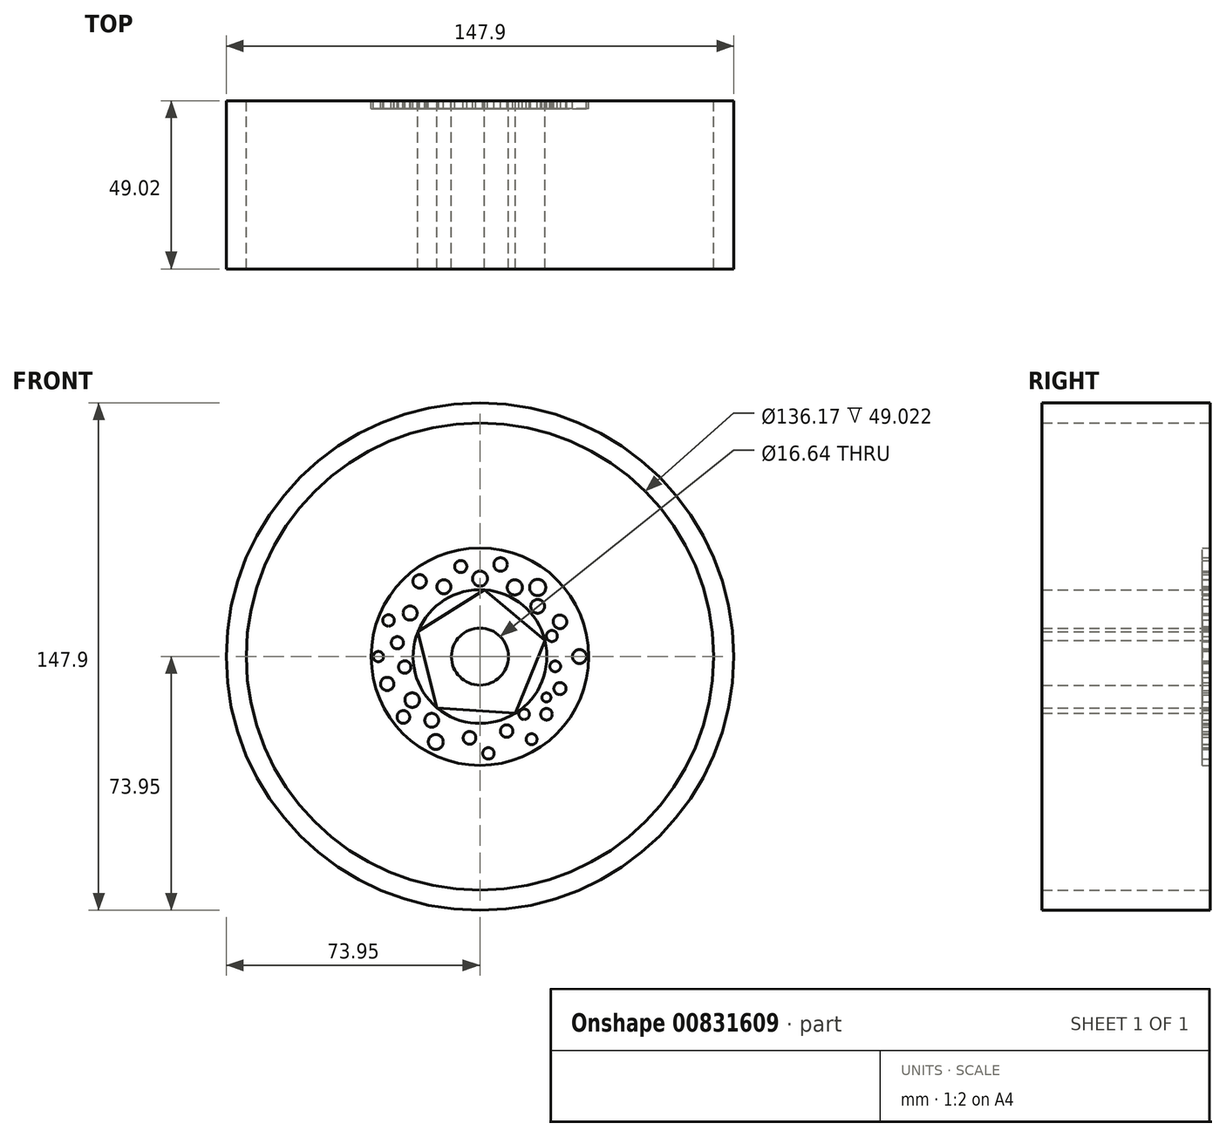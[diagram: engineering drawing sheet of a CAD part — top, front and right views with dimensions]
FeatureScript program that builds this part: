
annotation { "Feature Type Name" : "Feature", "Feature Type Description" : "" }
export const myFeature = defineFeature(function(context is Context, id is Id, definition is map)
    precondition{}
    {
        {
            var Q0;
            Q0=qCreatedBy(makeId("Front.planeOp"),FACE);
            var sketch = newSketch(context, id + "F0", { "sketchPlane" : qUnion([Q0])});
            skCircle(sketch, "E0", {"center": v(0, 0) * mm, "radius": 73.95 * mm});
            skCircle(sketch, "E1", {"center": v(0, 0) * mm, "radius": 68.08 * mm});
            skCircle(sketch, "E2.cCircle", {"center": v(0, 0) * mm, "radius": 15.77 * mm, "construction": true});
            skLineSegment(sketch, "E2.0", {"start": v(1.34, 19.45) * mm, "end": v(18.91, 4.73) * mm});
            skLineSegment(sketch, "E2.1", {"start": v(18.91, 4.73) * mm, "end": v(10.35, -16.52) * mm});
            skLineSegment(sketch, "E2.2", {"start": v(10.35, -16.52) * mm, "end": v(-12.52, -14.95) * mm});
            skLineSegment(sketch, "E2.3", {"start": v(-12.52, -14.95) * mm, "end": v(-18.08, 7.29) * mm});
            skLineSegment(sketch, "E2.4", {"start": v(-18.08, 7.29) * mm, "end": v(1.34, 19.45) * mm});
            skPoint(sketch, "E2.0.midPoint", {"position": v(10.13, 12.1) * mm});
            skPoint(sketch, "E3.orphan", {"position": v(68.08, 0) * mm});
            skPoint(sketch, "E4.end.orphan", {"position": v(0, 68.08) * mm});
            skCircle(sketch, "E5", {"center": v(0, 0) * mm, "radius": 8.32 * mm});
            skLineSegment(sketch, "E6", {"start": v(-2.6, 16.99) * mm, "end": v(12, 67.02) * mm});
            skLineSegment(sketch, "E7", {"start": v(6.2, 15.37) * mm, "end": v(14.3, 66.56) * mm});
            skLineSegment(sketch, "E8", {"start": v(14.3, 66.56) * mm, "end": v(12, 67.02) * mm});
            skLineSegment(sketch, "E9", {"start": v(-4.16, 16) * mm, "end": v(-31.83, 60.18) * mm});
            skLineSegment(sketch, "E10", {"start": v(-31.83, 60.18) * mm, "end": v(-34.5, 58.7) * mm});
            skLineSegment(sketch, "E11", {"start": v(-34.5, 58.7) * mm, "end": v(-12.64, 10.7) * mm});
            skLineSegment(sketch, "E12", {"start": v(-14.83, 9.32) * mm, "end": v(-62, 28.13) * mm});
            skLineSegment(sketch, "E13", {"start": v(-62, 28.13) * mm, "end": v(-64.05, 23.1) * mm});
            skLineSegment(sketch, "E14", {"start": v(-64.05, 23.1) * mm, "end": v(-16.26, 0) * mm});
            skLineSegment(sketch, "E15", {"start": v(-15.3, -3.83) * mm, "end": v(-60.76, -30.73) * mm});
            skLineSegment(sketch, "E16", {"start": v(-60.76, -30.73) * mm, "end": v(-58.22, -35.3) * mm});
            skLineSegment(sketch, "E17", {"start": v(-58.22, -35.3) * mm, "end": v(-12.52, -14.95) * mm});
            skLineSegment(sketch, "E18", {"start": v(-8.89, -15.2) * mm, "end": v(-20.94, -64.78) * mm});
            skPoint(sketch, "E19.end.orphan", {"position": v(-16.26, -67.05) * mm});
            skLineSegment(sketch, "E20", {"start": v(-16.26, -66.11) * mm, "end": v(2.9, -16) * mm});
            skLineSegment(sketch, "E21", {"start": v(23.8, -63.79) * mm, "end": v(27.6, -62.24) * mm});
            skLineSegment(sketch, "E22", {"start": v(49.88, -46.34) * mm, "end": v(53.15, -42.55) * mm});
            skLineSegment(sketch, "E23", {"start": v(67.23, -10.73) * mm, "end": v(67.82, -6.04) * mm});
            skLineSegment(sketch, "E24", {"start": v(59.94, 32.29) * mm, "end": v(56.36, 38.2) * mm});
            skLineSegment(sketch, "E25", {"start": v(8.55, -16.4) * mm, "end": v(33.9, -59.05) * mm});
            skLineSegment(sketch, "E26", {"start": v(33.9, -59.05) * mm, "end": v(37.56, -56.78) * mm});
            skLineSegment(sketch, "E27", {"start": v(37.56, -56.78) * mm, "end": v(14.63, -5.9) * mm});
            skLineSegment(sketch, "E28", {"start": v(65.25, -19.44) * mm, "end": v(66.64, -13.93) * mm});
            skPoint(sketch, "E29.start.orphan", {"position": v(17, 0) * mm});
            skLineSegment(sketch, "E30", {"start": v(17, 0) * mm, "end": v(67.95, -4.28) * mm});
            skLineSegment(sketch, "E31", {"start": v(67.95, -4.28) * mm, "end": v(67.95, 4.28) * mm});
            skLineSegment(sketch, "E32", {"start": v(68.08, 0) * mm, "end": v(11.92, 10.59) * mm});
            skLineSegment(sketch, "E33", {"start": v(11.92, 10.59) * mm, "end": v(52.61, 43.22) * mm});
            skLineSegment(sketch, "E34", {"start": v(52.61, 43.22) * mm, "end": v(49.02, 47.24) * mm});
            skPoint(sketch, "E35.startSnap0", {"position": v(50.82, 45.23) * mm});
            skPoint(sketch, "E36.start.orphan", {"position": v(49.02, 45.23) * mm});
            skLineSegment(sketch, "E37", {"start": v(49.02, 47.24) * mm, "end": v(6.2, 15.37) * mm});
            skSolve(sketch);
        }
        {
            var Q0;
            Q0=makeQuery(id+"F0.imprint","IMPRINT",FACE,{"disambiguationData":[TD([[makeQuery(id+"F0.imprint","IMPRINT",EDGE,{"derivedFrom":sQuery(id+"F0.wireOp",EDGE,"E0")}),1.0]])]});
            var Q1;
            Q1=makeQuery(id+"F0.imprint","IMPRINT",FACE,{"disambiguationData":[TD([[makeQuery(id+"F0.imprint","IMPRINT",EDGE,{"derivedFrom":sQuery(id+"F0.wireOp",EDGE,"E5")}),-1.0]])]});
            extrude(context, id + "F1", {"entities" : qUnion([Q0, Q1]), "depth" : 49.02 * mm, "offsetDistance" : 25.4 * mm});
        }
        {
            var Q0;
            Q0=qCreatedBy(makeId("Front.planeOp"),FACE);
            var sketch = newSketch(context, id + "F2", { "sketchPlane" : qUnion([Q0])});
            skCircle(sketch, "E38", {"center": v(0, 0) * mm, "radius": 19.48 * mm});
            skCircle(sketch, "E39", {"center": v(0, 0) * mm, "radius": 31.7 * mm});
            skCircle(sketch, "E40", {"center": v(6, 26.83) * mm, "radius": 1.97 * mm});
            skCircle(sketch, "E41", {"center": v(10.12, 20.15) * mm, "radius": 2.2 * mm});
            skCircle(sketch, "E42", {"center": v(16.8, 14.65) * mm, "radius": 2.02 * mm});
            skCircle(sketch, "E43", {"center": v(16.8, 20.15) * mm, "radius": 2.37 * mm});
            skCircle(sketch, "E44", {"center": v(20.94, 6) * mm, "radius": 1.62 * mm});
            skCircle(sketch, "E45", {"center": v(23.3, 10.12) * mm, "radius": 1.98 * mm});
            skCircle(sketch, "E46", {"center": v(21.92, -2.85) * mm, "radius": 1.58 * mm});
            skCircle(sketch, "E47", {"center": v(29, 0) * mm, "radius": 2.05 * mm});
            skCircle(sketch, "E48", {"center": v(19.36, -11.9) * mm, "radius": 1.32 * mm});
            skCircle(sketch, "E49", {"center": v(23.3, -9.34) * mm, "radius": 1.77 * mm});
            skCircle(sketch, "E50", {"center": v(12.88, -16.8) * mm, "radius": 1.54 * mm});
            skCircle(sketch, "E51", {"center": v(19.36, -16.8) * mm, "radius": 1.68 * mm});
            skCircle(sketch, "E52", {"center": v(15.04, -24.08) * mm, "radius": 1.58 * mm});
            skCircle(sketch, "E53", {"center": v(7.77, -21.72) * mm, "radius": 1.81 * mm});
            skCircle(sketch, "E54", {"center": v(2.46, -28.2) * mm, "radius": 1.68 * mm});
            skCircle(sketch, "E55", {"center": v(-3.05, -23.69) * mm, "radius": 1.85 * mm});
            skCircle(sketch, "E56", {"center": v(-12.88, -24.87) * mm, "radius": 2.17 * mm});
            skCircle(sketch, "E57", {"center": v(-14.06, -18.58) * mm, "radius": 2.02 * mm});
            skCircle(sketch, "E58", {"center": v(-19.76, -12.68) * mm, "radius": 2.12 * mm});
            skCircle(sketch, "E59", {"center": v(-22.31, -17.6) * mm, "radius": 1.85 * mm});
            skCircle(sketch, "E60", {"center": v(-21.92, -3.05) * mm, "radius": 1.81 * mm});
            skCircle(sketch, "E61", {"center": v(-27.03, -7.96) * mm, "radius": 1.94 * mm});
            skCircle(sketch, "E62", {"center": v(-29.59, 0) * mm, "radius": 1.5 * mm});
            skCircle(sketch, "E63", {"center": v(-24.08, 4.03) * mm, "radius": 1.77 * mm});
            skCircle(sketch, "E64", {"center": v(-26.64, 10.52) * mm, "radius": 1.68 * mm});
            skCircle(sketch, "E65", {"center": v(-20.35, 12.68) * mm, "radius": 2.05 * mm});
            skCircle(sketch, "E66", {"center": v(0, 22.7) * mm, "radius": 2.18 * mm});
            skCircle(sketch, "E67", {"center": v(-5.6, 26.24) * mm, "radius": 1.77 * mm});
            skCircle(sketch, "E68", {"center": v(-10.52, 20.35) * mm, "radius": 2.05 * mm});
            skCircle(sketch, "E69", {"center": v(-17.6, 21.92) * mm, "radius": 1.97 * mm});
            skSolve(sketch);
        }
        {
            var Q0;
            Q0 = qSketchRegion(id + "F2", true);
            extrude(context, id + "F3", {"entities" : qUnion([Q0]), "operationType" : NewBodyOperationType.ADD, "depth" : 2.3 * mm, "offsetDistance" : 25.4 * mm});
        }
    });
